# Revit family: Serenity Series - Panel Wall - Surface Mounted
name_source: partatom
category: Generic Models
units: mm (PartAtom-declared; Revit-internal decimal feet)

## family parameters
Always vertical = Yes
Can host rebar = No
Cut with Voids When Loaded = No
Host = Wall
Part Type = Normal
Room Calculation Point = No
Round Connector Dimension = Use Diameter
Shared = No

## types (12) — shared parameters
Base Offset = 0' - 8"
Ceiling Height = 9' - 0"
Center Section = 3' - 11 1/2"
Manufacturer = Amico Corporation
Model = Serenity Series Surface Mounted Panel Wall
URL = https://www.amico.com
Unit Depth = 0' - 5"

## per-type parameters (varying)
| type | Full Frame Panel | Inside Rail | No Rail | Outside Rail | Panel - Inside Rail | Panel - No Rail | Panel - Outisde Rail | Side Section |
| 24 - 48 - 24 Full Frame | Yes | Yes | No | Yes | No | No | No | 1' - 11 1/2" |
| 24 - 48 - 24 - No Rail | No | No | Yes | No | No | Yes | No | 1' - 11 1/2" |
| 24 - 48 - 24 - Outside Rail | No | No | Yes | Yes | No | No | Yes | 1' - 11 1/2" |
| 24 - 48 - 24 - Inside Rail | No | Yes | Yes | No | Yes | No | No | 1' - 11 1/2" |
| 19 - 48 - 19 - Full Frame | Yes | Yes | No | Yes | No | No | No | 1' - 7" |
| 19 - 48 - 19 - No Rail | No | No | Yes | No | No | Yes | No | 1' - 7" |
| 19 - 48 - 19 - Outside Rail | No | No | Yes | Yes | No | No | Yes | 1' - 7" |
| 19 - 48 - 19 - Inside Rail | No | Yes | Yes | No | Yes | No | No | 1' - 7" |
| 32 - 48 - 32 - Full Frame | Yes | Yes | No | Yes | No | No | No | 2' - 8" |
| 32 - 48 - 32 - Inside Rail | No | Yes | Yes | No | Yes | No | No | 2' - 8" |
| 32 - 48 - 32 - No Rail | No | No | Yes | No | No | Yes | No | 2' - 8" |
| 32 - 48 - 32 - Outside Rail | No | No | Yes | Yes | No | No | Yes | 2' - 8" |

## geometry (parser evidence)
native form markers: Extrusion x14, Sweep x36
no freeform markers — native parametric forms only
